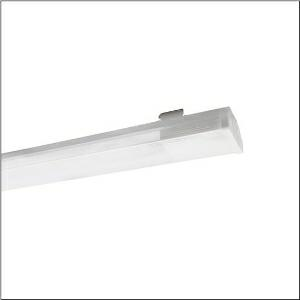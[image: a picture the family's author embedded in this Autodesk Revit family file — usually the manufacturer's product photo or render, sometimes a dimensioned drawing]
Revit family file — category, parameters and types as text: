
# Revit family: modario_r__31_gen_2_53bm8137u4l3d2_98c8
name_source: partatom
category: Lighting Fixtures
units: mm (PartAtom-declared; Revit-internal decimal feet)

## family parameters
Cut with Voids When Loaded = No
Host = Face
Light Source = No
Part Type = Normal
Room Calculation Point = No
Round Connector Dimension = Use Diameter
Shared = No

## types (1)
- Modario® 31 Gen.2 (1 x LED, 23060 lm, 126 W, 4000K)
    Apparent Load = 126 VA
    CIE Flux Codes = 62 83 95 93 100
    Color Rendering = 80
    Color Temperature = 4000K
    Default Elevation = 1800 mm
    Description = Modario® 31 Gen.2, luminaire insert, of sheet steel, coil coated, white, length: 2.392mm, width: 81mm, height: 82mm, 8x system unit, system units: 299mm, LED rated luminous flux: 23.060lm, light colour: 840, control gear: ON/OFF, with plug, 3-pole, with phase selection, mains connection: 220..240V, AC, 50/60Hz, rated input power: 126W, through-wiring accessed according to module size, primary optical cover: cover, of PMMA, light emission: direct distribution, primary light characteristic: symmetric, protection rating (complete): IP20, protection rating (LED compartment): IP50, insulation class (complete): insulation class I (protective earthing), certification: CE, ENEC, VDE, UKCA, impact resistance: IK03, permissible ambient temperature for indoor applications: -40..+35°C, corresponds to IFS (International Featured Standards) requirements for safety and quality in the food industry, reducing of maximum allowable ambient temperature of 5°C with ceiling mounting, packaging unit: 1 piece
    Height = 92 mm
    Lamp = 1 x LED
    Lamp Light Flux = 23060 lm
    Lamp Power = 126 W
    Lamp count = 1
    Length = 2392 mm
    Luminous efficacy = 183 lm/W
    Manufacturer = Siteco
    ModVariant = No
    Model = 53BM8137U4L3D2
    Mounting Place = Ceiling
    Mounting Type = Pendant
    Number of Poles = 1
    OnlyDefault = Yes
    Power Factor = 1
    Product Name = Modario® 31 Gen.2
    Product group = luminaire insert
    ProductGroupID = 902
    Protection Class = Protection class I
    Protection Degree = IP 20
    RLX_Detail_Level = 1
    RLX_Emergency_Light_Flux = 0 lm
    RLX_Emergency_Type = 0
    RLX_Emergency_Type_DB = No
    RlxData = <blob elided: 34697 chars, md5=2d28d17e>
    Socket = socket
    Standby Power = 0 W
    System Light Flux = 23061 lm
    System Power = 126 W
    Type Comments = Product without accessories
    Type Image = l_1341883.jpg
    URL = http://relux.com
    VarID = ---
    Voltage = 0 V
    Weight = 0.00 kg
    Width = 81 mm

## geometry (parser evidence)
native form markers: Blend x4, Sweep x13
no freeform markers — native parametric forms only
